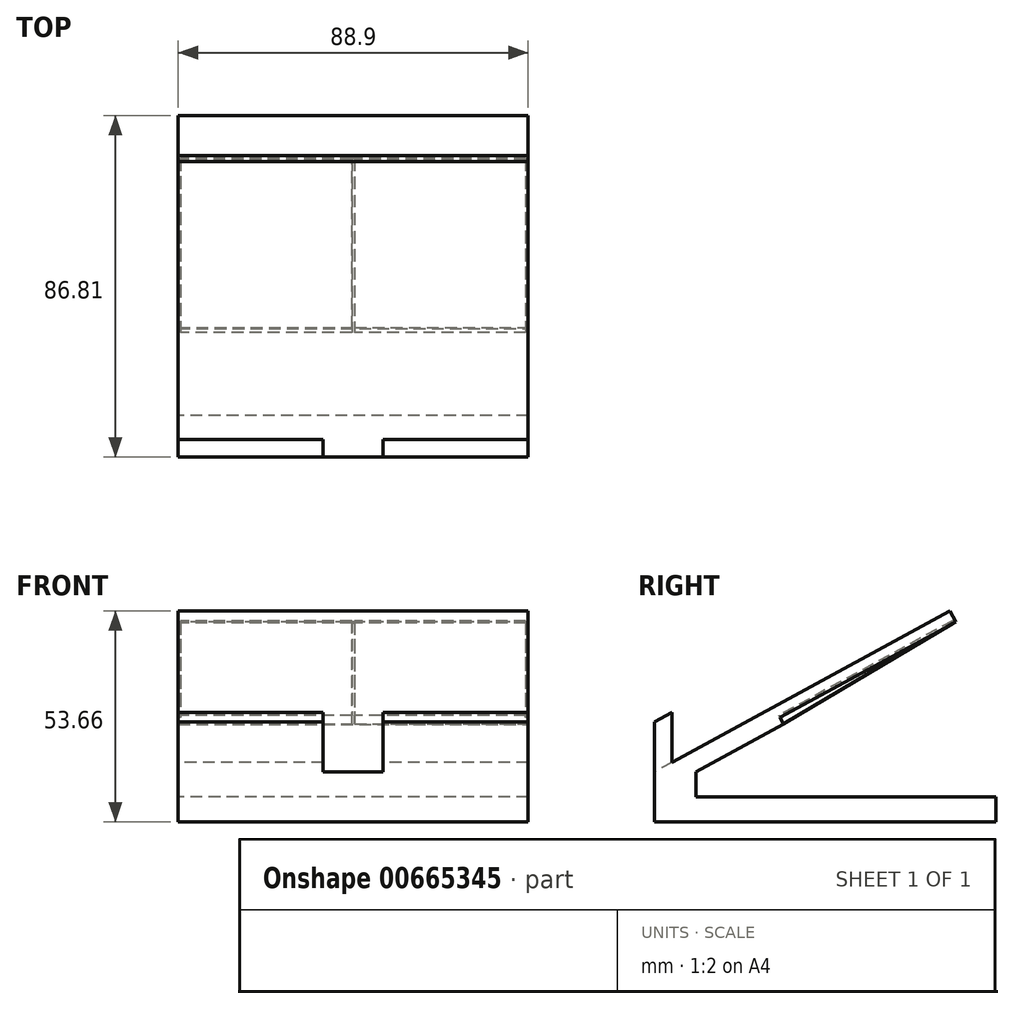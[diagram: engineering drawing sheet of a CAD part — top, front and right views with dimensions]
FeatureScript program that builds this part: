
annotation { "Feature Type Name" : "Feature", "Feature Type Description" : "" }
export const myFeature = defineFeature(function(context is Context, id is Id, definition is map)
    precondition{}
    {
        {
            var Q0;
            Q0=qCreatedBy(makeId("Right.planeOp"),FACE);
            var sketch = newSketch(context, id + "F0", { "sketchPlane" : qUnion([Q0])});
            skLineSegment(sketch, "E0", {"start": v(0, 0) * mm, "end": v(-86.8, 0) * mm});
            skLineSegment(sketch, "E1", {"start": v(-86.8, 0) * mm, "end": v(-86.8, 12.7) * mm});
            skLineSegment(sketch, "E2", {"start": v(-86.8, 12.7) * mm, "end": v(-56.34, 29.32) * mm});
            skLineSegment(sketch, "E3", {"start": v(-56.34, 29.32) * mm, "end": v(-53.9, 24.87) * mm});
            skLineSegment(sketch, "E4", {"start": v(-53.9, 24.87) * mm, "end": v(-76.2, 12.7) * mm});
            skLineSegment(sketch, "E5", {"start": v(-86.8, 12.7) * mm, "end": v(-86.8, 25.4) * mm});
            skLineSegment(sketch, "E6", {"start": v(-86.8, 25.4) * mm, "end": v(-82.35, 27.83) * mm});
            skLineSegment(sketch, "E7", {"start": v(-82.35, 27.83) * mm, "end": v(-82.35, 15.13) * mm});
            skLineSegment(sketch, "E8", {"start": v(0, 0) * mm, "end": v(0, 6.35) * mm});
            skLineSegment(sketch, "E9", {"start": v(0, 6.35) * mm, "end": v(-76.2, 6.35) * mm});
            skLineSegment(sketch, "E10", {"start": v(-76.2, 6.35) * mm, "end": v(-76.2, 12.7) * mm});
            skLineSegment(sketch, "E11", {"start": v(-55.12, 27.1) * mm, "end": v(-10.53, 51.43) * mm});
            skLineSegment(sketch, "E12", {"start": v(-10.53, 51.43) * mm, "end": v(-11.74, 53.66) * mm});
            skLineSegment(sketch, "E13", {"start": v(-11.74, 53.66) * mm, "end": v(-56.34, 29.32) * mm});
            skSolve(sketch);
        }
        {
            var Q0;
            Q0 = qSketchRegion(id + "F0", true);
            extrude(context, id + "F1", {"entities" : qUnion([Q0]), "depth" : 88.9 * mm, "offsetDistance" : 25.4 * mm});
        }
        {
            var Q0;
            Q0=makeQuery(id+"F1.opExtrude","SWEPT_FACE",FACE,{"disambiguationData":[OSD([sQuery(id+"F0.wireOp",EDGE,"E1"),sQuery(id+"F0.wireOp",EDGE,"E5")])]});
            var sketch = newSketch(context, id + "F2", { "sketchPlane" : qUnion([Q0])});
            skLineSegment(sketch, "E14", {"start": v(36.83, 28.15) * mm, "end": v(52.07, 28.15) * mm});
            skLineSegment(sketch, "E15", {"start": v(36.83, 28.15) * mm, "end": v(36.83, 12.4) * mm});
            skLineSegment(sketch, "E16", {"start": v(36.83, 12.4) * mm, "end": v(52.07, 12.4) * mm});
            skLineSegment(sketch, "E17", {"start": v(52.07, 12.4) * mm, "end": v(52.07, 28.15) * mm});
            skSolve(sketch);
        }
        {
            var Q0;
            Q0 = qSketchRegion(id + "F2", true);
            var Q1;
            Q1=makeQuery(id+"F1.opExtrude","SWEPT_FACE",FACE,{"disambiguationData":[OSD([sQuery(id+"F0.wireOp",EDGE,"E2")])]});
            extrude(context, id + "F3", {"entities" : qUnion([Q0]), "operationType" : NewBodyOperationType.REMOVE, "endBound" : BoundingType.UP_TO_SURFACE, "oppositeDirection" : true, "depth" : 25.4 * mm, "endBoundEntityFace" : qUnion([Q1]), "offsetDistance" : 25.4 * mm});
        }
        {
            var Q0;
            Q0=makeQuery(id+"F1.opExtrude","SWEPT_FACE",FACE,{"disambiguationData":[OSD([sQuery(id+"F0.wireOp",EDGE,"E11")])]});
            var sketch = newSketch(context, id + "F4", { "sketchPlane" : qUnion([Q0])});
            skLineSegment(sketch, "E18", {"start": v(88.9, -15.4) * mm, "end": v(88.9, 35.4) * mm});
            skLineSegment(sketch, "E19", {"start": v(88.9, 35.4) * mm, "end": v(0, 35.4) * mm});
            skLineSegment(sketch, "E20", {"start": v(0, 35.4) * mm, "end": v(0, -15.4) * mm});
            skLineSegment(sketch, "E21", {"start": v(0, -15.4) * mm, "end": v(88.9, -15.4) * mm});
            skLineSegment(sketch, "E22", {"start": v(88.27, -14.76) * mm, "end": v(44.77, -14.76) * mm});
            skLineSegment(sketch, "E23", {"start": v(44.13, -14.76) * mm, "end": v(0.64, -14.76) * mm});
            skLineSegment(sketch, "E24", {"start": v(88.27, -14.76) * mm, "end": v(88.27, 35.4) * mm});
            skLineSegment(sketch, "E25", {"start": v(44.77, -14.76) * mm, "end": v(44.77, 35.4) * mm});
            skLineSegment(sketch, "E26", {"start": v(44.13, -14.76) * mm, "end": v(44.13, 35.4) * mm});
            skLineSegment(sketch, "E27", {"start": v(0.64, -14.76) * mm, "end": v(0.64, 35.4) * mm});
            skLineSegment(sketch, "E28", {"start": v(44.77, -14.76) * mm, "end": v(44.13, -14.76) * mm});
            skSolve(sketch);
        }
        {
            var Q0;
            Q0=makeQuery(id+"F4.imprint","IMPRINT",FACE,{"disambiguationData":[TD([[makeQuery(id+"F4.imprint","IMPRINT",EDGE,{"derivedFrom":sQuery(id+"F4.wireOp",EDGE,"E18")}),-1.0]])]});
            var Q1;
            {var subQ0=sQuery(id+"F4.wireOp",EDGE,"E25");Q1=makeQuery(id+"F4.imprint","IMPRINT",FACE,{"disambiguationData":[TD([[makeQuery(id+"F4.imprint","IMPRINT",EDGE,{"derivedFrom":subQ0}),1.0]])]});}
            extrude(context, id + "F5", {"entities" : qUnion([Q0, Q1]), "operationType" : NewBodyOperationType.ADD, "depth" : 0.64 * mm, "offsetDistance" : 25.4 * mm});
        }
        {
            var Q0;
            Q0=makeQuery(id+"F1.opExtrude","SWEPT_FACE",FACE,{"disambiguationData":[OSD([sQuery(id+"F0.wireOp",EDGE,"E3")])]});
            var sketch = newSketch(context, id + "F6", { "sketchPlane" : qUnion([Q0])});
            skLineSegment(sketch, "E29", {"start": v(-44.13, 49.55) * mm, "end": v(-44.13, 47.65) * mm});
            skPoint(sketch, "E29.endSnap0", {"position": v(-44.45, 47.65) * mm});
            skLineSegment(sketch, "E30", {"start": v(-44.77, 49.55) * mm, "end": v(-44.77, 47.65) * mm});
            skSolve(sketch);
        }
        {
            var Q0;
            {var subQ0=sQuery(id+"F6.wireOp",EDGE,"E29");Q0=makeQuery(id+"F6.imprint","IMPRINT",FACE,{"disambiguationData":[TD([[makeQuery(id+"F6.imprint","IMPRINT",EDGE,{"derivedFrom":subQ0}),-1.0]])]});}
            var Q1;
            Q1=makeQuery(id+"F5.boolean.opBoolean","MERGE",FACE,{"derivedFrom":[makeQuery(id+"F1.opExtrude","SWEPT_FACE",FACE,{"disambiguationData":[OSD([sQuery(id+"F0.wireOp",EDGE,"E12")])]}),makeQuery(id+"F5.opExtrude","SWEPT_FACE",FACE,{"disambiguationData":[OSD([sQuery(id+"F4.wireOp",EDGE,"E21")])]})]});
            extrude(context, id + "F7", {"entities" : qUnion([Q0]), "operationType" : NewBodyOperationType.ADD, "depth" : 49.96 * mm, "endBoundEntityFace" : qUnion([Q1]), "offsetDistance" : 25.4 * mm});
        }
        {
            var Q0;
            Q0=makeQuery(id+"F7.opExtrude","CAP_EDGE",EDGE,{"disambiguationData":[OSD([sQuery(id+"F0.wireOp",EDGE,"E3"),sQuery(id+"F0.wireOp",EDGE,"E4")])],"isStart":false});
            chamfer(context, id + "F8", {"entities" : qUnion([Q0]), "chamferType" : ChamferType.TWO_OFFSETS, "width1" : 1.9 * mm, "oppositeDirection" : false, "width2" : 50.16 * mm, "tangentPropagation" : true});
        }
    });
